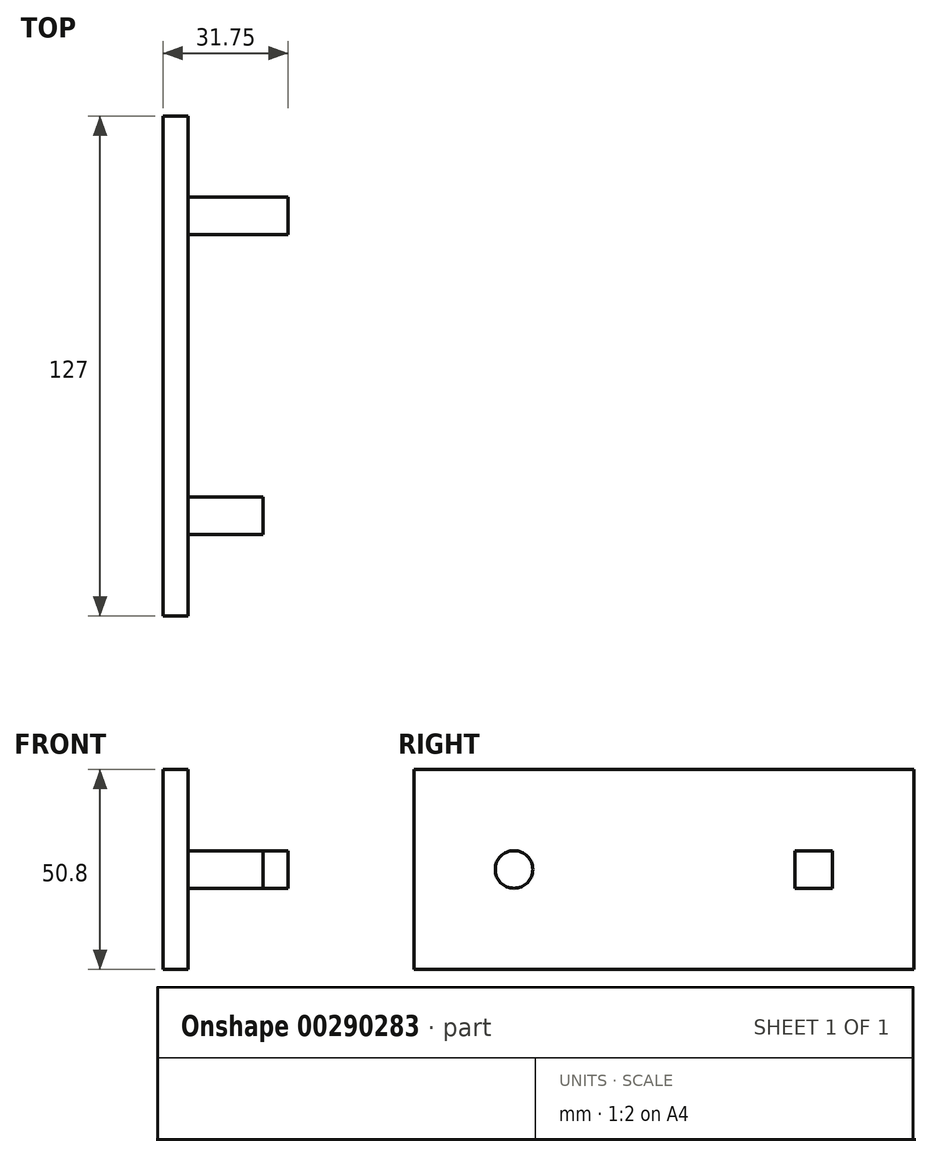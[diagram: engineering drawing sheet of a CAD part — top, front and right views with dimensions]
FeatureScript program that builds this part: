
annotation { "Feature Type Name" : "Feature", "Feature Type Description" : "" }
export const myFeature = defineFeature(function(context is Context, id is Id, definition is map)
    precondition{}
    {
        {
            var Q0;
            Q0=qCreatedBy(makeId("Right.planeOp"),FACE);
            var sketch = newSketch(context, id + "F0", { "sketchPlane" : qUnion([Q0])});
            skLineSegment(sketch, "E0.bottom", {"start": v(63.5, -25.4) * mm, "end": v(-63.5, -25.4) * mm});
            skLineSegment(sketch, "E0.top", {"start": v(63.5, 25.4) * mm, "end": v(-63.5, 25.4) * mm});
            skLineSegment(sketch, "E0.left", {"start": v(63.5, -25.4) * mm, "end": v(63.5, 25.4) * mm});
            skLineSegment(sketch, "E0.right", {"start": v(-63.5, -25.4) * mm, "end": v(-63.5, 25.4) * mm});
            skPoint(sketch, "E0.middle", {"position": v(0, 0) * mm});
            skSolve(sketch);
        }
        {
            var Q0;
            Q0 = qSketchRegion(id + "F0", true);
            extrude(context, id + "F1", {"entities" : qUnion([Q0]), "depth" : 6.35 * mm});
        }
        {
            var Q0;
            Q0=makeQuery(id+"F1.opExtrude","CAP_FACE",FACE,{"disambiguationData":[OSD([sQuery(id+"F0.wireOp",EDGE,"E0.bottom"),sQuery(id+"F0.wireOp",EDGE,"E0.top"),sQuery(id+"F0.wireOp",EDGE,"E0.left"),sQuery(id+"F0.wireOp",EDGE,"E0.right")])],"isStart":false});
            var sketch = newSketch(context, id + "F2", { "sketchPlane" : qUnion([Q0])});
            skLineSegment(sketch, "E1", {"start": v(-63.5, 25.4) * mm, "end": v(-38.1, 25.4) * mm});
            skCircle(sketch, "E2", {"center": v(-38.1, 0) * mm, "radius": 4.76 * mm});
            skLineSegment(sketch, "E3", {"start": v(63.5, 25.4) * mm, "end": v(38.1, 25.4) * mm});
            skLineSegment(sketch, "E4.bottom", {"start": v(42.86, -4.76) * mm, "end": v(33.34, -4.76) * mm});
            skLineSegment(sketch, "E4.top", {"start": v(42.86, 4.76) * mm, "end": v(33.34, 4.76) * mm});
            skLineSegment(sketch, "E4.left", {"start": v(42.86, -4.76) * mm, "end": v(42.86, 4.76) * mm});
            skLineSegment(sketch, "E4.right", {"start": v(33.34, -4.76) * mm, "end": v(33.34, 4.76) * mm});
            skPoint(sketch, "E4.middle", {"position": v(38.1, 0) * mm});
            skSolve(sketch);
        }
        {
            var Q0;
            Q0 = qSketchRegion(id + "F2", true);
            extrude(context, id + "F3", {"entities" : qUnion([Q0]), "operationType" : NewBodyOperationType.ADD, "depth" : 19.05 * mm});
        }
        {
            var Q0;
            Q0=makeQuery(id+"F3.opExtrude","CAP_FACE",FACE,{"disambiguationData":[OSD([sQuery(id+"F2.wireOp",EDGE,"E4.bottom"),sQuery(id+"F2.wireOp",EDGE,"E4.top"),sQuery(id+"F2.wireOp",EDGE,"E4.left"),sQuery(id+"F2.wireOp",EDGE,"E4.right")])],"isStart":false});
            extrude(context, id + "F4", {"entities" : qUnion([Q0]), "operationType" : NewBodyOperationType.ADD, "depth" : 6.35 * mm});
        }
    });
